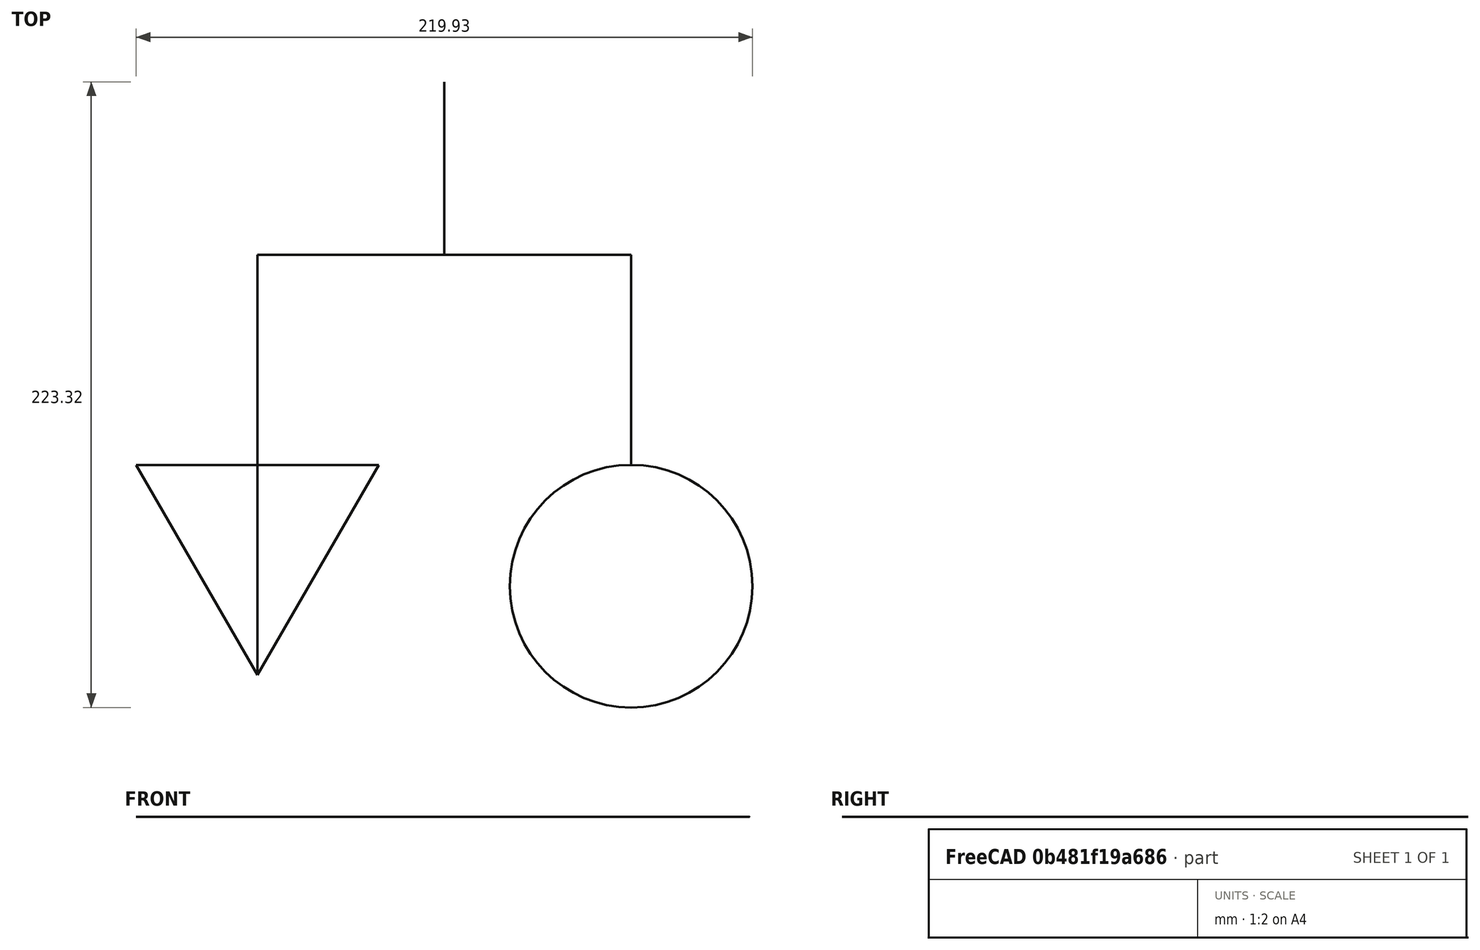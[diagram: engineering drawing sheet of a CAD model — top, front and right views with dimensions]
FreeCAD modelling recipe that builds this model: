
FCSTD DOCUMENT  (FreeCAD 1.1R20260325 (Git shallow))
Label: Interruptor_Tomada_Media_1modulo_220v_com_simbologia
License: All rights reserved
LicenseURL: http://en.wikipedia.org/wiki/All_rights_reserved
objects: Part::FeaturePython×1, Part::Feature×1, App::DocumentObjectGroup×1
note: 2 computed .brp shape members not serialized (recipe doc carries the construction recipe); baked Part::Feature solids carry a one-line shape summary decoded from their .brp

FEATURE [Part::FeaturePython] Component  label="Interruptor_Tomada_110v_media"  # Arch/BIM 0 (typed FeaturePython)
  HorizontalArea = 0
  IfcData = attributes={"GlobalId": {"name": "GlobalId", "type": "IfcGloballyUniqueId", "is_enum": false, "enum_values": []}, "Description": {"... (+538 chars omitted),+1 more (map truncated)
  IfcType = 0
  MoveBase = false
  MoveWithHost = false
  PerimeterLength = 0
  Placement = pos=(0,0,1200) rot=(0,0,1;0rad)
  PredefinedType = 0
  VerticalArea = 0
FEATURE [Part::Feature] Compound002002002004005002002003003002003005002002005002002002002002002002002002002002  label="Simbologia_Tomada_Interruptor"
  Placement = pos=(804.665,1993.94,1191.87) rot=(0,0,-1;1.5708rad)
  shape: bbox 219.9 x 223.3 x 2e-07 mm, 1 faces, 0 solids (baked)
FEATURE [App::DocumentObjectGroup] Group  label="Interruptor_Tomada_media"
  Group = -> [Component,Compound002002002004005002002003003002003005002002005002002002002002002002002002002002]
